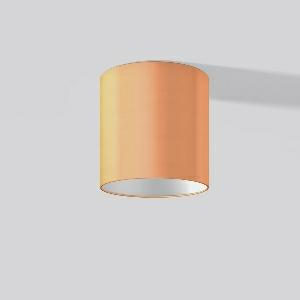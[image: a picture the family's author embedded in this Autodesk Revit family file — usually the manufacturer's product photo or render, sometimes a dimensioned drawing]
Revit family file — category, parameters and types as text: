
# Revit family: toledo_flatliner_901632_002_1_76_d823
name_source: partatom
category: Lighting Fixtures
units: mm (PartAtom-declared; Revit-internal decimal feet)

## family parameters
Cut with Voids When Loaded = No
Host = Face
Light Source = No
Part Type = Normal
Room Calculation Point = No
Round Connector Dimension = Use Diameter
Shared = No

## types (1)
- 982301.002 (1 x LED Modul 840, 1400 lm, 4000)
    Apparent Load = 17 VA
    CIE Flux Codes = 50 82 97 99 100
    Color Rendering = 80
    Color Temperature = 4000
    Default Elevation = 1800 mm
    Description = Series: TOLEDO FLATLINER
Decorative ceiling luminaire for interior decoration. Base luminaire prepared for the installation of fabric lampshade. Cylinder housing sheet steel, powder-coated. Housing: die cast aluminium and sheet steel, powder-coated. Bezel ring: die-cast aluminium, powder-coated. Lightguide and diffuser made of non-yellowing plastic (PMMA) opal matt. Modular design: With the basic luminaire, a square or cylindrical fabric lampshade must always be ordered separately. Fabric lampshades can be fitted to the basic luminaire without tools. Order satin finish diffuser as separate accessory. 
Colour: white
Diameter: 268 mm
Height: 70 mm
Lamp: LED
Socket: without socket
Colour temperature: 4000K
Colour rendering index (CRI): 80
System power: 17 W
Rated luminous flux: 1400 lm
Luminous efficiency: 82 lm/W
Control gear: Converter, dimmable, DALI
Protection class: II
Type of protection: IP 40
    Height = 70 mm
    Lamp = 1 x LED Modul 840
    Lamp Light Flux = 1400 lm
    Lamp count = 1
    Length = 268 mm
    Lifetime = 50000 h
    Luminous efficacy = 82 lm/W
    Manufacturer = RZB
    ModVariant = No
    Model = 901632.002.1.76
    Mounting Place = Ceiling
    Mounting Type = Surface mounted
    Number of Poles = 1
    OnlyDefault = Yes
    Power Factor = 1
    Product Name = TOLEDO FLATLINER
    Product group = Surface mounted ceiling Fabric lampshade luminaires
    ProductGroupID = 313
    Protection Class = Protection class II
    Protection Degree = IP 40
    RLX_Detail_Level = 1
    RLX_Emergency_Light_Flux = 0 lm
    RLX_Emergency_Type = 0
    RLX_Emergency_Type_DB = No
    RlxData = <blob elided: 62713 chars, md5=88a63245>
    Socket = socket
    Standby Power = 0 W
    System Light Flux = 1400 lm
    System Power = 17 W
    Type Image = toledo_flatliner_anbau_rund_orange_odeckel.jpg
    URL = http://relux.com
    VarID = 982301_002_5b69
    Voltage = 230 V
    Voltage Range = 220-240 V
    Weight = 0.00 kg
    Width = 0 mm  [stored 0 ft]

note: [stored X ft] marks values corroborated as IEEE doubles in the binary element streams (Revit-internal decimal feet)

## geometry (parser evidence)
native form markers: Blend x4, Sweep x8
no freeform markers — native parametric forms only
